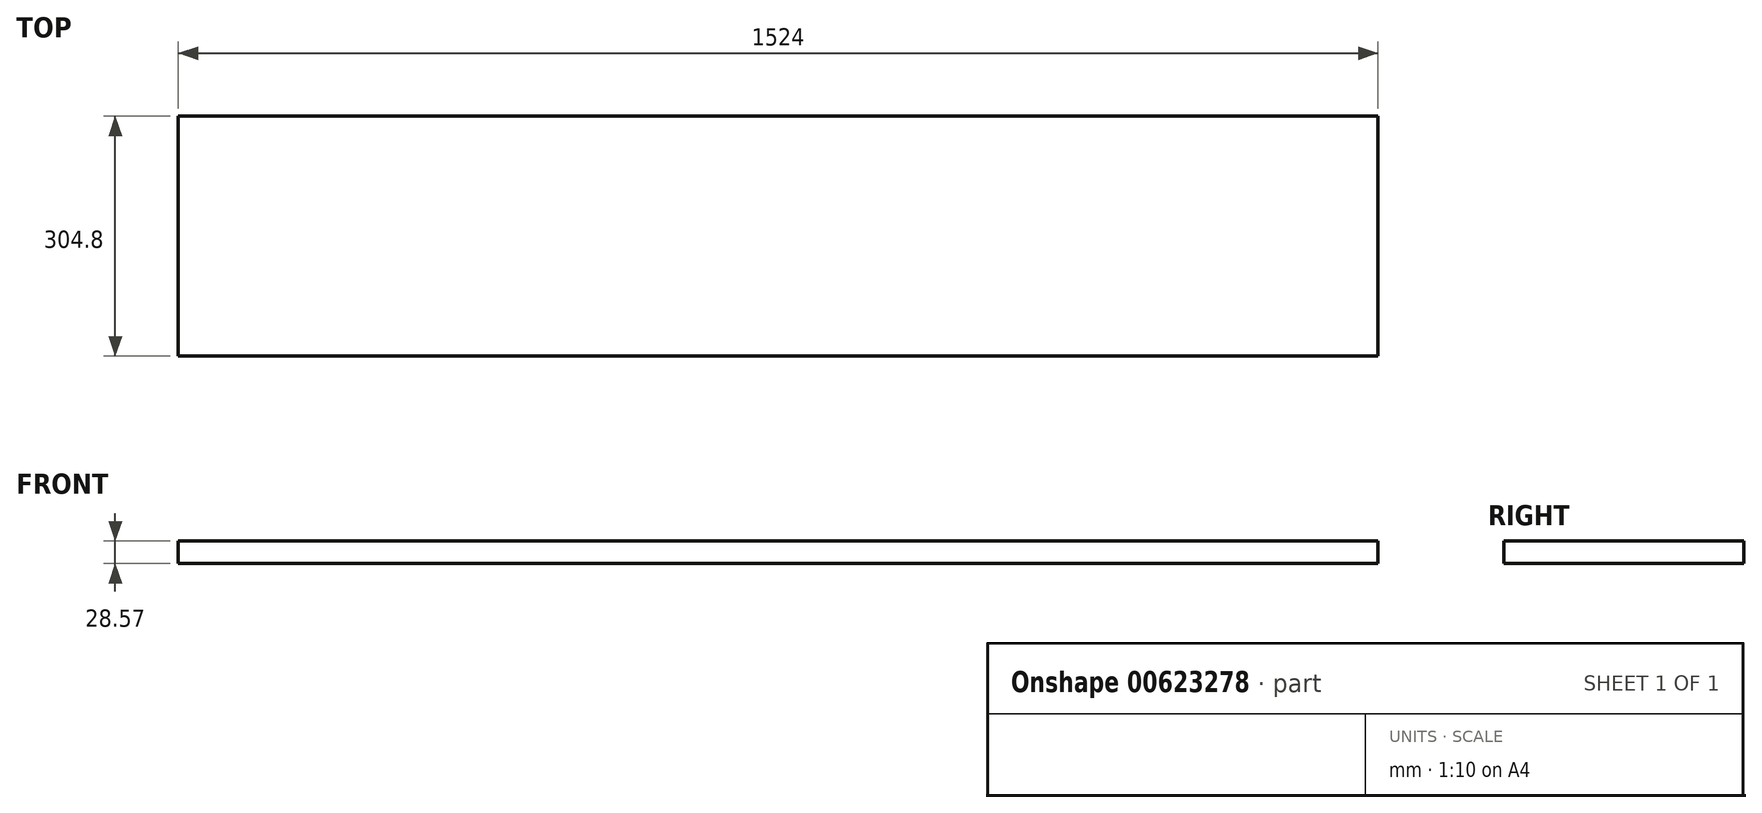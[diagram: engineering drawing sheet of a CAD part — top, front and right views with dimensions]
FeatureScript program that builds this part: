
annotation { "Feature Type Name" : "Feature", "Feature Type Description" : "" }
export const myFeature = defineFeature(function(context is Context, id is Id, definition is map)
    precondition{}
    {
        {
            var Q0;
            Q0=qCreatedBy(makeId("Top.planeOp"),FACE);
            var sketch = newSketch(context, id + "F0", { "sketchPlane" : qUnion([Q0])});
            skLineSegment(sketch, "E0.bottom", {"start": v(762, 152.4) * mm, "end": v(-762, 152.4) * mm});
            skLineSegment(sketch, "E0.top", {"start": v(762, -152.4) * mm, "end": v(-762, -152.4) * mm});
            skLineSegment(sketch, "E0.left", {"start": v(762, 152.4) * mm, "end": v(762, -152.4) * mm});
            skLineSegment(sketch, "E0.right", {"start": v(-762, 152.4) * mm, "end": v(-762, -152.4) * mm});
            skPoint(sketch, "E0.middle", {"position": v(0, 0) * mm});
            skSolve(sketch);
        }
        {
            var Q0;
            Q0=makeQuery(id+"F0.imprint","IMPRINT",FACE,{"disambiguationData":[TD([[makeQuery(id+"F0.imprint","IMPRINT",EDGE,{"derivedFrom":sQuery(id+"F0.wireOp",EDGE,"E0.bottom")}),1.0]])]});
            extrude(context, id + "F1", {"entities" : qUnion([Q0]), "depth" : 28.57 * mm, "offsetDistance" : 25.4 * mm});
        }
    });
